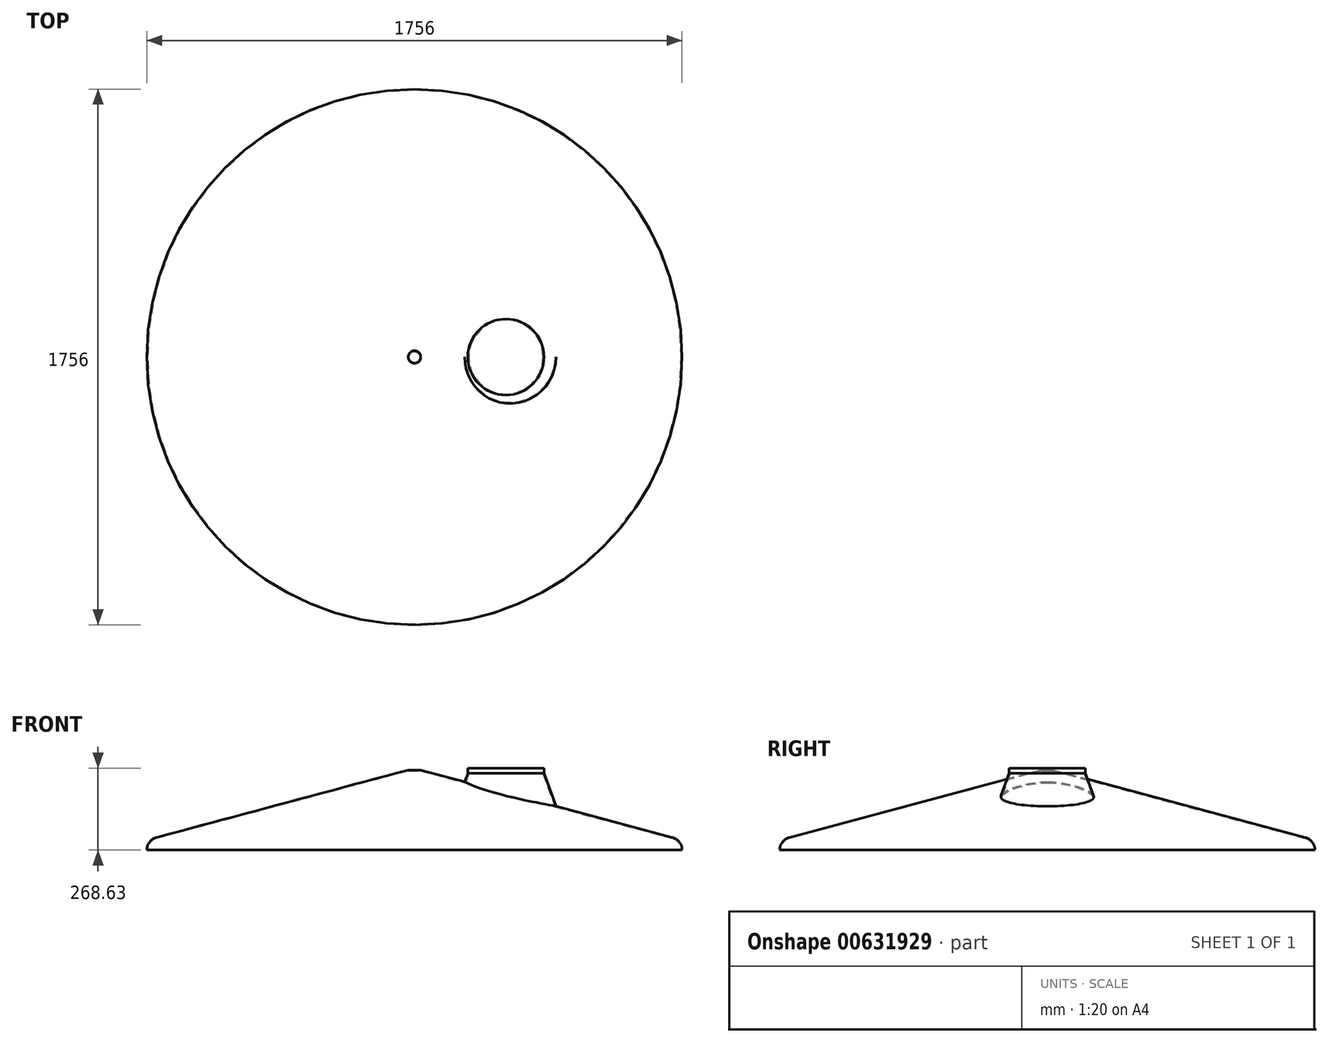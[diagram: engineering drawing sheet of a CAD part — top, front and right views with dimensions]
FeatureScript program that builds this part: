
annotation { "Feature Type Name" : "Feature", "Feature Type Description" : "" }
export const myFeature = defineFeature(function(context is Context, id is Id, definition is map)
    precondition{}
    {
        {
            var Q0;
            Q0=qCreatedBy(makeId("Front.planeOp"),FACE);
            var sketch = newSketch(context, id + "F0", { "sketchPlane" : qUnion([Q0])});
            skArc(sketch, "E0", {"start": v(878, 0) * mm, "mid": v(869.11, 26.18) * mm, "end": v(846.13, 41.53) * mm});
            skLineSegment(sketch, "E1", {"start": v(846.13, 41.53) * mm, "end": v(20.78, 262.69) * mm});
            skLineSegment(sketch, "E2.0", {"start": v(845.35, 38.64) * mm, "end": v(20, 259.79) * mm});
            skArc(sketch, "E3.0", {"start": v(875, 0) * mm, "mid": v(866.73, 24.35) * mm, "end": v(845.35, 38.64) * mm});
            skLineSegment(sketch, "E4", {"start": v(20.78, 262.69) * mm, "end": v(20, 259.79) * mm});
            skLineSegment(sketch, "E5", {"start": v(875, 0) * mm, "end": v(878, 0) * mm});
            skLineSegment(sketch, "E6", {"start": v(0, 0) * mm, "end": v(0, 290.69) * mm, "construction": true});
            skSolve(sketch);
        }
        {
            var Q0;
            Q0=makeQuery(id+"F0.imprint","IMPRINT",FACE,{"disambiguationData":[TD([[makeQuery(id+"F0.imprint","IMPRINT",EDGE,{"derivedFrom":sQuery(id+"F0.wireOp",EDGE,"E0")}),1.0]])]});
            var Q1;
            Q1=sQuery(id+"F0.wireOp",EDGE,"E6");
            var Q2;
            Q2=sQuery(id+"F0.wireOp",EDGE,"E6");
            revolve(context, id + "F1", {"entities" : qUnion([Q0]), "surfaceEntities" : qUnion([Q1]), "axis" : qUnion([Q2]), "revolveType" : RevolveType.FULL});
        }
        {
            var Q0;
            Q0=qCreatedBy(makeId("Front.planeOp"),FACE);
            var sketch = newSketch(context, id + "F2", { "sketchPlane" : qUnion([Q0])});
            skLineSegment(sketch, "E7", {"start": v(300, 252) * mm, "end": v(425, 252) * mm});
            skLineSegment(sketch, "E8", {"start": v(425, 252) * mm, "end": v(516.72, 0) * mm});
            skLineSegment(sketch, "E9", {"start": v(516.72, 0) * mm, "end": v(300, 0) * mm});
            skLineSegment(sketch, "E10", {"start": v(300, 252) * mm, "end": v(300, 0) * mm});
            skSolve(sketch);
        }
        {
            var Q0;
            Q0=makeQuery(id+"F2.imprint","IMPRINT",FACE,{"disambiguationData":[TD([[makeQuery(id+"F2.imprint","IMPRINT",EDGE,{"derivedFrom":sQuery(id+"F2.wireOp",EDGE,"E7")}),-1.0]])]});
            var Q1;
            Q1=sQuery(id+"F2.wireOp",EDGE,"E10");
            revolve(context, id + "F3", {"operationType" : NewBodyOperationType.REMOVE, "entities" : qUnion([Q0]), "axis" : qUnion([Q1]), "revolveType" : RevolveType.FULL, "oppositeDirection" : true});
        }
        {
            var Q0;
            Q0=qCreatedBy(makeId("Front.planeOp"),FACE);
            var sketch = newSketch(context, id + "F4", { "sketchPlane" : qUnion([Q0])});
            skLineSegment(sketch, "E11.0", {"start": v(425, 252) * mm, "end": v(516.72, 0) * mm});
            skLineSegment(sketch, "E12.0", {"start": v(421.24, 250.63) * mm, "end": v(512.96, -1.37) * mm});
            skLineSegment(sketch, "E13", {"start": v(516.72, 0) * mm, "end": v(512.96, -1.37) * mm});
            skLineSegment(sketch, "E14", {"start": v(425, 252) * mm, "end": v(425, 268.63) * mm});
            skLineSegment(sketch, "E15", {"start": v(425, 268.63) * mm, "end": v(300, 268.63) * mm});
            skLineSegment(sketch, "E16", {"start": v(421.24, 250.63) * mm, "end": v(300, 250.63) * mm});
            skLineSegment(sketch, "E17", {"start": v(300, 250.63) * mm, "end": v(300, 268.63) * mm});
            skSolve(sketch);
        }
        {
            var Q0;
            Q0=makeQuery(id+"F4.imprint","IMPRINT",FACE,{"disambiguationData":[TD([[makeQuery(id+"F4.imprint","IMPRINT",EDGE,{"derivedFrom":sQuery(id+"F4.wireOp",EDGE,"E11.0")}),-1.0]])]});
            var Q1;
            Q1=sQuery(id+"F4.wireOp",EDGE,"E17");
            revolve(context, id + "F5", {"operationType" : NewBodyOperationType.ADD, "entities" : qUnion([Q0]), "axis" : qUnion([Q1]), "revolveType" : RevolveType.FULL});
        }
        {
            var Q0;
            Q0=qCreatedBy(makeId("Front.planeOp"),FACE);
            var sketch = newSketch(context, id + "F6", { "sketchPlane" : qUnion([Q0])});
            skLineSegment(sketch, "E18.0", {"start": v(544.78, 119.18) * mm, "end": v(60, 249.07) * mm});
            skLineSegment(sketch, "E19", {"start": v(0, 0) * mm, "end": v(0, 295.01) * mm});
            skLineSegment(sketch, "E20", {"start": v(60, 249.07) * mm, "end": v(60, -66.78) * mm});
            skLineSegment(sketch, "E21", {"start": v(60, -66.78) * mm, "end": v(544.78, -66.78) * mm});
            skLineSegment(sketch, "E22", {"start": v(544.78, -66.78) * mm, "end": v(544.78, 119.18) * mm});
            skSolve(sketch);
        }
        {
            var Q0;
            Q0=makeQuery(id+"F6.imprint","IMPRINT",FACE,{"disambiguationData":[TD([[makeQuery(id+"F6.imprint","IMPRINT",EDGE,{"derivedFrom":sQuery(id+"F6.wireOp",EDGE,"E18.0")}),1.0]])]});
            var Q1;
            Q1=sQuery(id+"F6.wireOp",EDGE,"E19");
            revolve(context, id + "F7", {"operationType" : NewBodyOperationType.REMOVE, "entities" : qUnion([Q0]), "axis" : qUnion([Q1]), "revolveType" : RevolveType.FULL, "oppositeDirection" : true});
        }
    });
